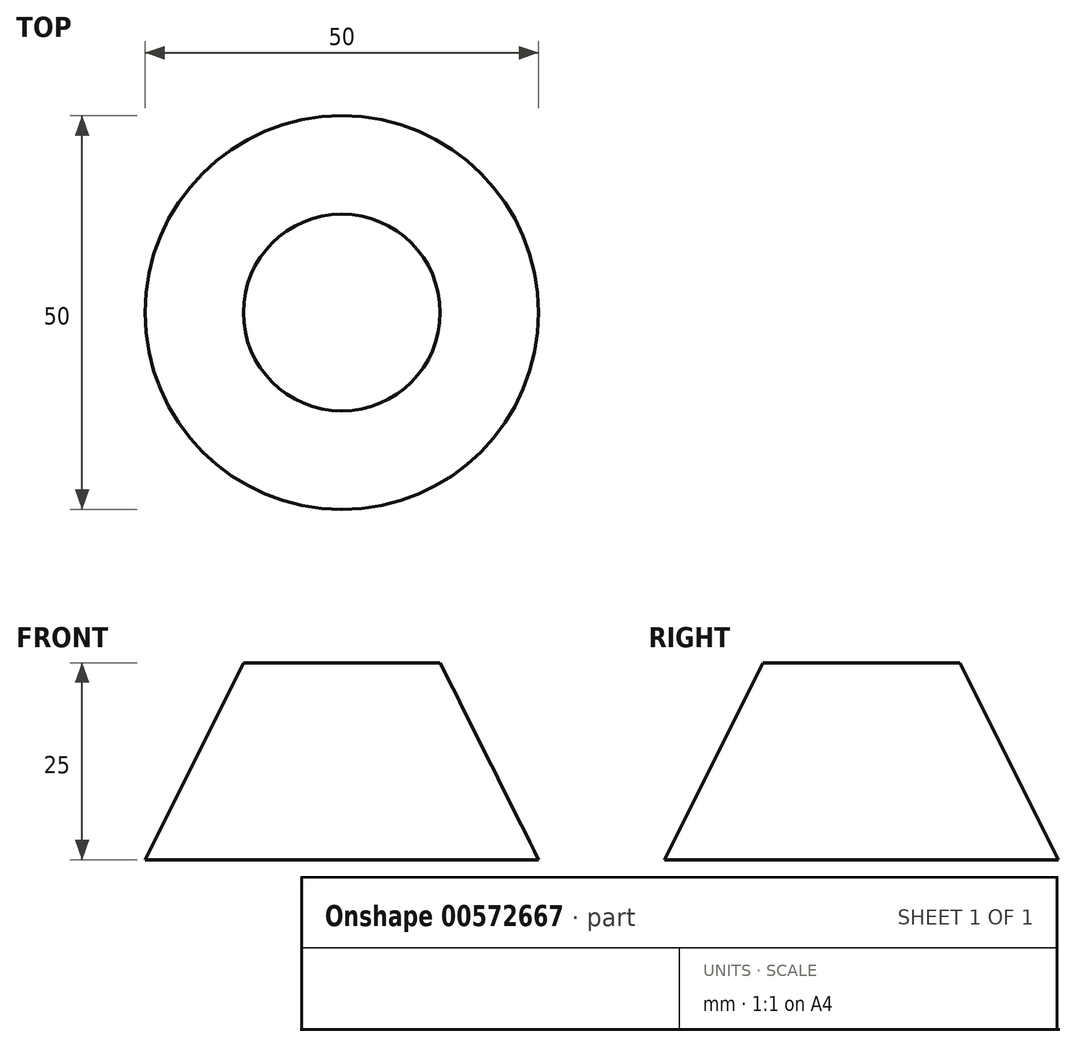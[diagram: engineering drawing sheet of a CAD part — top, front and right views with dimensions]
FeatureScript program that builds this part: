
annotation { "Feature Type Name" : "Feature", "Feature Type Description" : "" }
export const myFeature = defineFeature(function(context is Context, id is Id, definition is map)
    precondition{}
    {
        {
            var Q0;
            Q0=qCreatedBy(makeId("Top.planeOp"),FACE);
            var sketch = newSketch(context, id + "F0", { "sketchPlane" : qUnion([Q0])});
            skCircle(sketch, "E0", {"center": v(0, 0) * mm, "radius": 25 * mm});
            skSolve(sketch);
        }
        {
            var Q0;
            Q0=qCreatedBy(makeId("Top.planeOp"),FACE);
            cPlane(context, id + "F1", {"entities" : qUnion([Q0]), "cplaneType" : CPlaneType.OFFSET, "offset" : 25 * mm, "width" : 150 * mm, "height" : 150 * mm});
        }
        {
            var Q0;
            Q0=qCreatedBy(id+"F1.planeOp",FACE);
            var sketch = newSketch(context, id + "F2", { "sketchPlane" : qUnion([Q0])});
            skCircle(sketch, "E1", {"center": v(0, 0) * mm, "radius": 12.5 * mm});
            skSolve(sketch);
        }
        {
            var Q0;
            Q0=makeQuery(id+"F2.imprint","IMPRINT",FACE,{"disambiguationData":[TD([[makeQuery(id+"F2.imprint","IMPRINT",EDGE,{"derivedFrom":sQuery(id+"F2.wireOp",EDGE,"E1")}),1.0]])]});
            var Q1;
            Q1=makeQuery(id+"F0.imprint","IMPRINT",FACE,{"disambiguationData":[TD([[makeQuery(id+"F0.imprint","IMPRINT",EDGE,{"derivedFrom":sQuery(id+"F0.wireOp",EDGE,"E0")}),1.0]])]});
            loft(context, id + "F3", {"sheetProfilesArray" : [{ "sheetProfileEntities" : qUnion([Q0]) }, { "sheetProfileEntities" : qUnion([Q1]) }]});
        }
    });
